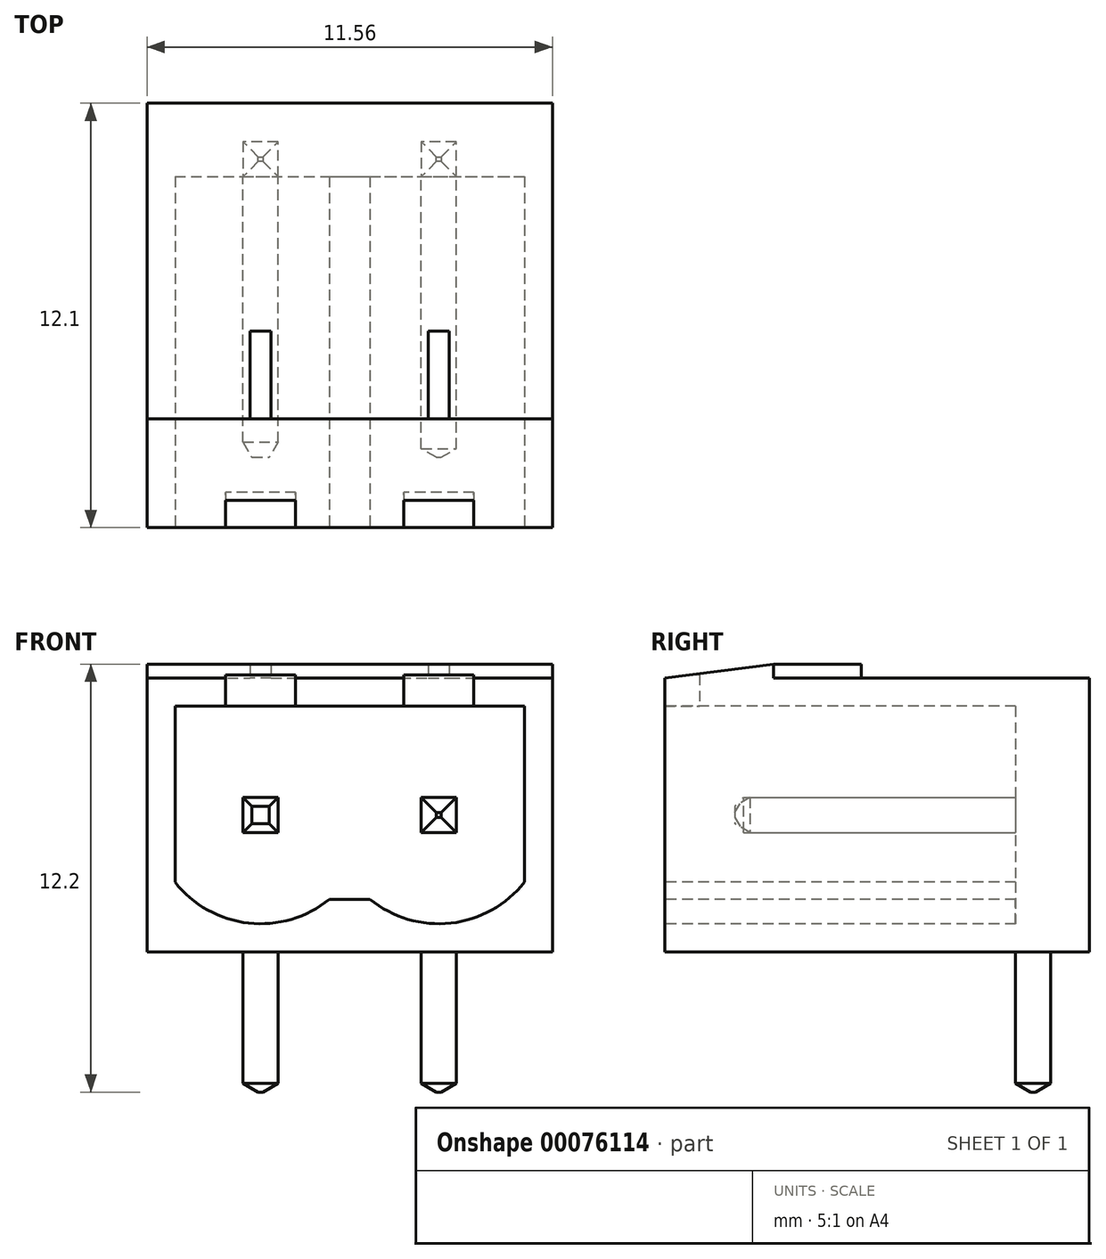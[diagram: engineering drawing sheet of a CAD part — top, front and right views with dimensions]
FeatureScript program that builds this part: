
annotation { "Feature Type Name" : "Feature", "Feature Type Description" : "" }
export const myFeature = defineFeature(function(context is Context, id is Id, definition is map)
    precondition{}
    {
        {
            var Q0;
            Q0=qCreatedBy(makeId("Top.planeOp"),FACE);
            var sketch = newSketch(context, id + "F0", { "sketchPlane" : qUnion([Q0])});
            skLineSegment(sketch, "E0.bottom", {"start": v(-5.78, 6.05) * mm, "end": v(5.78, 6.05) * mm});
            skLineSegment(sketch, "E0.top", {"start": v(-5.78, -6.05) * mm, "end": v(5.78, -6.05) * mm});
            skLineSegment(sketch, "E0.left", {"start": v(-5.78, 6.05) * mm, "end": v(-5.78, -6.05) * mm});
            skLineSegment(sketch, "E0.right", {"start": v(5.78, 6.05) * mm, "end": v(5.78, -6.05) * mm});
            skPoint(sketch, "E0.middle", {"position": v(0, 0) * mm});
            skSolve(sketch);
        }
        {
            var Q0;
            Q0 = qSketchRegion(id + "F0", true);
            extrude(context, id + "F1", {"entities" : qUnion([Q0]), "depth" : 8.2 * mm});
        }
        {
            var Q0;
            Q0=makeQuery(id+"F1.opExtrude","SWEPT_FACE",FACE,{"disambiguationData":[OSD([sQuery(id+"F0.wireOp",EDGE,"E0.top")])]});
            var sketch = newSketch(context, id + "F2", { "sketchPlane" : qUnion([Q0])});
            skLineSegment(sketch, "E1.bottom", {"start": v(-4.98, 7) * mm, "end": v(4.98, 7) * mm});
            skLineSegment(sketch, "E1.top", {"start": v(-2.54, 0.8) * mm, "end": v(2.54, 0.8) * mm, "construction": true});
            skLineSegment(sketch, "E1.left", {"start": v(-4.98, 7) * mm, "end": v(-4.98, 1.99) * mm});
            skLineSegment(sketch, "E1.right", {"start": v(4.98, 7) * mm, "end": v(4.98, 1.99) * mm});
            skPoint(sketch, "E1.middle", {"position": v(0, 4.1) * mm});
            skPoint(sketch, "E1.middle.positionSnap0", {"position": v(0, 8.2) * mm});
            skPoint(sketch, "E1.middle.positionSnap1", {"position": v(-5.78, 4.1) * mm});
            skPoint(sketch, "E1.centerSnap0", {"position": v(0, 8.2) * mm});
            skPoint(sketch, "E1.centerSnap1", {"position": v(-5.78, 4.1) * mm});
            skArc(sketch, "E2", {"start": v(-4.98, 1.99) * mm, "mid": v(-2.88, 0.82) * mm, "end": v(-0.58, 1.5) * mm});
            skPoint(sketch, "E2.centerSnap0", {"position": v(-4.98, 3.9) * mm});
            skArc(sketch, "E3", {"start": v(0.58, 1.5) * mm, "mid": v(2.88, 0.82) * mm, "end": v(4.98, 1.99) * mm});
            skPoint(sketch, "E3.centerSnap0", {"position": v(4.98, 3.9) * mm});
            skLineSegment(sketch, "E4", {"start": v(-2.54, 3.9) * mm, "end": v(2.54, 3.9) * mm, "construction": true});
            skLineSegment(sketch, "E5", {"start": v(0, 3.9) * mm, "end": v(0, 7) * mm, "construction": true});
            skPoint(sketch, "E6.orphan", {"position": v(-4.98, 0.8) * mm});
            skPoint(sketch, "E7.orphan", {"position": v(4.98, 0.8) * mm});
            skLineSegment(sketch, "E8", {"start": v(-0.58, 1.5) * mm, "end": v(0.58, 1.5) * mm});
            skSolve(sketch);
        }
        {
            var Q0;
            Q0 = qSketchRegion(id + "F2", true);
            extrude(context, id + "F3", {"entities" : qUnion([Q0]), "operationType" : NewBodyOperationType.REMOVE, "oppositeDirection" : true, "depth" : 10 * mm});
        }
        {
            var Q0;
            Q0=makeQuery(id+"F3.boolean.opBoolean","COPY",FACE,{"derivedFrom":makeQuery(id+"F3.opExtrude","CAP_FACE",FACE,{"disambiguationData":[OSD([sQuery(id+"F2.wireOp",EDGE,"E1.bottom"),sQuery(id+"F2.wireOp",EDGE,"E1.left"),sQuery(id+"F2.wireOp",EDGE,"E1.right"),sQuery(id+"F2.wireOp",EDGE,"E2"),sQuery(id+"F2.wireOp",EDGE,"E3"),sQuery(id+"F2.wireOp",EDGE,"E8")])],"isStart":false})});
            var sketch = newSketch(context, id + "F4", { "sketchPlane" : qUnion([Q0])});
            skLineSegment(sketch, "E9.bottom", {"start": v(-2.04, 4.4) * mm, "end": v(-3.04, 4.4) * mm});
            skLineSegment(sketch, "E9.top", {"start": v(-2.04, 3.4) * mm, "end": v(-3.04, 3.4) * mm});
            skLineSegment(sketch, "E9.left", {"start": v(-2.04, 4.4) * mm, "end": v(-2.04, 3.4) * mm});
            skLineSegment(sketch, "E9.right", {"start": v(-3.04, 4.4) * mm, "end": v(-3.04, 3.4) * mm});
            skPoint(sketch, "E9.middle", {"position": v(-2.54, 3.9) * mm});
            skLineSegment(sketch, "E10.bottom", {"start": v(2.04, 4.4) * mm, "end": v(3.04, 4.4) * mm});
            skLineSegment(sketch, "E10.top", {"start": v(2.04, 3.4) * mm, "end": v(3.04, 3.4) * mm});
            skLineSegment(sketch, "E10.left", {"start": v(2.04, 4.4) * mm, "end": v(2.04, 3.4) * mm});
            skLineSegment(sketch, "E10.right", {"start": v(3.04, 4.4) * mm, "end": v(3.04, 3.4) * mm});
            skPoint(sketch, "E10.middle", {"position": v(2.54, 3.9) * mm});
            skSolve(sketch);
        }
        {
            var Q0;
            Q0 = qSketchRegion(id + "F4", true);
            extrude(context, id + "F5", {"entities" : qUnion([Q0]), "depth" : 8 * mm});
        }
        {
            var Q0;
            Q0=makeQuery(id+"F1.opExtrude","CAP_FACE",FACE,{"disambiguationData":[OSD([sQuery(id+"F0.wireOp",EDGE,"E0.bottom"),sQuery(id+"F0.wireOp",EDGE,"E0.top"),sQuery(id+"F0.wireOp",EDGE,"E0.left"),sQuery(id+"F0.wireOp",EDGE,"E0.right")])],"isStart":true});
            var sketch = newSketch(context, id + "F6", { "sketchPlane" : qUnion([Q0])});
            skPoint(sketch, "E11.centerSnap0", {"position": v(-5.78, 0) * mm});
            skPoint(sketch, "E12.centerSnap0", {"position": v(5.78, 0) * mm});
            skLineSegment(sketch, "E13", {"start": v(-2.54, -4.45) * mm, "end": v(2.54, -4.45) * mm, "construction": true});
            skLineSegment(sketch, "E14", {"start": v(0, -4.45) * mm, "end": v(0, -6.05) * mm, "construction": true});
            skLineSegment(sketch, "E15.bottom", {"start": v(-3.04, -3.95) * mm, "end": v(-2.04, -3.95) * mm});
            skLineSegment(sketch, "E15.top", {"start": v(-3.04, -4.95) * mm, "end": v(-2.04, -4.95) * mm});
            skLineSegment(sketch, "E15.left", {"start": v(-3.04, -3.95) * mm, "end": v(-3.04, -4.95) * mm});
            skLineSegment(sketch, "E15.right", {"start": v(-2.04, -3.95) * mm, "end": v(-2.04, -4.95) * mm});
            skPoint(sketch, "E15.middle", {"position": v(-2.54, -4.45) * mm});
            skLineSegment(sketch, "E16.bottom", {"start": v(2.04, -3.95) * mm, "end": v(3.04, -3.95) * mm});
            skLineSegment(sketch, "E16.top", {"start": v(2.04, -4.95) * mm, "end": v(3.04, -4.95) * mm});
            skLineSegment(sketch, "E16.left", {"start": v(2.04, -3.95) * mm, "end": v(2.04, -4.95) * mm});
            skLineSegment(sketch, "E16.right", {"start": v(3.04, -3.95) * mm, "end": v(3.04, -4.95) * mm});
            skPoint(sketch, "E16.middle", {"position": v(2.54, -4.45) * mm});
            skSolve(sketch);
        }
        {
            var Q0;
            Q0 = qSketchRegion(id + "F6", true);
            extrude(context, id + "F7", {"entities" : qUnion([Q0]), "depth" : 4 * mm});
        }
        {
            var Q0;
            Q0=makeQuery(id+"F1.opExtrude","SWEPT_FACE",FACE,{"disambiguationData":[OSD([sQuery(id+"F0.wireOp",EDGE,"E0.right")])]});
            var sketch = newSketch(context, id + "F8", { "sketchPlane" : qUnion([Q0])});
            skLineSegment(sketch, "E17.bottom", {"start": v(6.05, 8.2) * mm, "end": v(-2.95, 8.2) * mm});
            skLineSegment(sketch, "E17.top", {"start": v(6.05, 7.8) * mm, "end": v(-2.95, 7.8) * mm});
            skLineSegment(sketch, "E17.left", {"start": v(6.05, 8.2) * mm, "end": v(6.05, 7.8) * mm});
            skLineSegment(sketch, "E17.right", {"start": v(-2.95, 8.2) * mm, "end": v(-2.95, 7.8) * mm});
            skLineSegment(sketch, "E18", {"start": v(-6.05, 7.8) * mm, "end": v(-2.95, 8.2) * mm});
            skLineSegment(sketch, "E19", {"start": v(-6.05, 8.2) * mm, "end": v(-6.05, 7.8) * mm});
            skLineSegment(sketch, "E20", {"start": v(-6.05, 8.2) * mm, "end": v(-2.95, 8.2) * mm});
            skSolve(sketch);
        }
        {
            var Q0;
            Q0 = qSketchRegion(id + "F8", true);
            extrude(context, id + "F9", {"entities" : qUnion([Q0]), "operationType" : NewBodyOperationType.REMOVE, "oppositeDirection" : true, "depth" : 25 * mm});
        }
        {
            var Q0;
            Q0=makeQuery(id+"F5.opExtrude","CAP_FACE",FACE,{"disambiguationData":[OSD([sQuery(id+"F4.wireOp",EDGE,"E10.bottom"),sQuery(id+"F4.wireOp",EDGE,"E10.top"),sQuery(id+"F4.wireOp",EDGE,"E10.left"),sQuery(id+"F4.wireOp",EDGE,"E10.right")])],"isStart":false});
            var Q1;
            Q1=makeQuery(id+"F5.opExtrude","CAP_FACE",FACE,{"disambiguationData":[OSD([sQuery(id+"F4.wireOp",EDGE,"E9.bottom"),sQuery(id+"F4.wireOp",EDGE,"E9.top"),sQuery(id+"F4.wireOp",EDGE,"E9.left"),sQuery(id+"F4.wireOp",EDGE,"E9.right")])],"isStart":false});
            var Q2;
            Q2=makeQuery(id+"F7.opExtrude","CAP_FACE",FACE,{"disambiguationData":[OSD([sQuery(id+"F6.wireOp",EDGE,"E16.bottom"),sQuery(id+"F6.wireOp",EDGE,"E16.top"),sQuery(id+"F6.wireOp",EDGE,"E16.left"),sQuery(id+"F6.wireOp",EDGE,"E16.right")])],"isStart":false});
            var Q3;
            Q3=makeQuery(id+"F7.opExtrude","CAP_FACE",FACE,{"disambiguationData":[OSD([sQuery(id+"F6.wireOp",EDGE,"E15.bottom"),sQuery(id+"F6.wireOp",EDGE,"E15.top"),sQuery(id+"F6.wireOp",EDGE,"E15.left"),sQuery(id+"F6.wireOp",EDGE,"E15.right")])],"isStart":false});
            chamfer(context, id + "F10", {"entities" : qUnion([Q0, Q1, Q2, Q3]), "chamferType" : ChamferType.OFFSET_ANGLE, "width" : 0.25 * mm, "oppositeDirection" : false, "angle" : 60 * degree, "tangentPropagation" : true});
        }
        {
            var Q0;
            Q0=makeQuery(id+"F1.opExtrude","SWEPT_FACE",FACE,{"disambiguationData":[OSD([sQuery(id+"F0.wireOp",EDGE,"E0.top")])]});
            var sketch = newSketch(context, id + "F11", { "sketchPlane" : qUnion([Q0])});
            skLineSegment(sketch, "E21.bottom", {"start": v(-1.54, 7.9) * mm, "end": v(-3.54, 7.9) * mm});
            skLineSegment(sketch, "E21.top", {"start": v(-1.54, 6.9) * mm, "end": v(-3.54, 6.9) * mm});
            skLineSegment(sketch, "E21.left", {"start": v(-1.54, 7.9) * mm, "end": v(-1.54, 6.9) * mm});
            skLineSegment(sketch, "E21.right", {"start": v(-3.54, 7.9) * mm, "end": v(-3.54, 6.9) * mm});
            skPoint(sketch, "E21.middle", {"position": v(-2.54, 7.4) * mm});
            skLineSegment(sketch, "E22", {"start": v(-2.54, 3.9) * mm, "end": v(-2.54, 7.8) * mm, "construction": true});
            skLineSegment(sketch, "E23.bottom", {"start": v(3.54, 7.9) * mm, "end": v(1.54, 7.9) * mm});
            skLineSegment(sketch, "E23.top", {"start": v(3.54, 6.9) * mm, "end": v(1.54, 6.9) * mm});
            skLineSegment(sketch, "E23.left", {"start": v(3.54, 7.9) * mm, "end": v(3.54, 6.9) * mm});
            skLineSegment(sketch, "E23.right", {"start": v(1.54, 7.9) * mm, "end": v(1.54, 6.9) * mm});
            skPoint(sketch, "E23.middle", {"position": v(2.54, 7.4) * mm});
            skSolve(sketch);
        }
        {
            var Q0;
            Q0 = qSketchRegion(id + "F11", true);
            extrude(context, id + "F12", {"entities" : qUnion([Q0]), "operationType" : NewBodyOperationType.REMOVE, "oppositeDirection" : true, "depth" : 1 * mm});
        }
        {
            var Q0;
            Q0=makeQuery(id+"F9.boolean.opBoolean","COPY",FACE,{"derivedFrom":makeQuery(id+"F9.opExtrude","SWEPT_FACE",FACE,{"disambiguationData":[OSD([sQuery(id+"F8.wireOp",EDGE,"E17.top")])]})});
            var sketch = newSketch(context, id + "F13", { "sketchPlane" : qUnion([Q0])});
            skLineSegment(sketch, "E24.bottom", {"start": v(-2.24, -2.95) * mm, "end": v(-2.84, -2.95) * mm});
            skLineSegment(sketch, "E24.top", {"start": v(-2.24, -0.45) * mm, "end": v(-2.84, -0.45) * mm});
            skLineSegment(sketch, "E24.left", {"start": v(-2.24, -2.95) * mm, "end": v(-2.24, -0.45) * mm});
            skLineSegment(sketch, "E24.right", {"start": v(-2.84, -2.95) * mm, "end": v(-2.84, -0.45) * mm});
            skPoint(sketch, "E24.middle", {"position": v(-2.54, -1.7) * mm});
            skLineSegment(sketch, "E25", {"start": v(-2.54, -2.95) * mm, "end": v(-2.54, -5.27) * mm, "construction": true});
            skPoint(sketch, "E25.endSnap0", {"position": v(-2.54, -2.95) * mm});
            skLineSegment(sketch, "E26.bottom", {"start": v(2.24, -0.45) * mm, "end": v(2.84, -0.45) * mm});
            skLineSegment(sketch, "E26.top", {"start": v(2.24, -2.95) * mm, "end": v(2.84, -2.95) * mm});
            skLineSegment(sketch, "E26.left", {"start": v(2.24, -0.45) * mm, "end": v(2.24, -2.95) * mm});
            skLineSegment(sketch, "E26.right", {"start": v(2.84, -0.45) * mm, "end": v(2.84, -2.95) * mm});
            skPoint(sketch, "E26.middle", {"position": v(2.54, -1.7) * mm});
            skSolve(sketch);
        }
        {
            var Q0;
            Q0 = qSketchRegion(id + "F13", true);
            extrude(context, id + "F14", {"entities" : qUnion([Q0]), "operationType" : NewBodyOperationType.ADD, "depth" : 0.4 * mm});
        }
    });
